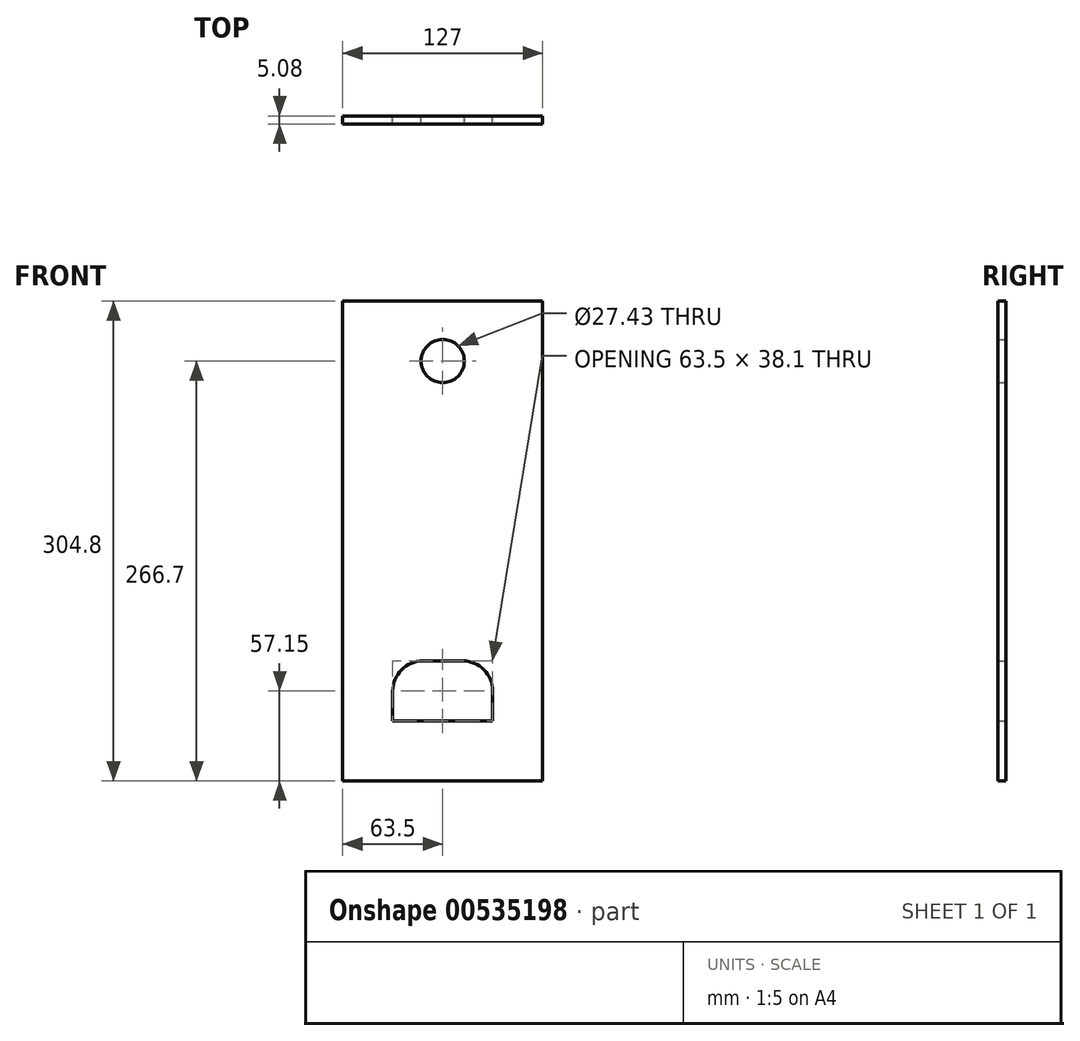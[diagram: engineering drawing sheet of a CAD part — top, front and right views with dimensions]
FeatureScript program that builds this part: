
annotation { "Feature Type Name" : "Feature", "Feature Type Description" : "" }
export const myFeature = defineFeature(function(context is Context, id is Id, definition is map)
    precondition{}
    {
        {
            var Q0;
            Q0=qCreatedBy(makeId("Front.planeOp"),FACE);
            var sketch = newSketch(context, id + "F0", { "sketchPlane" : qUnion([Q0])});
            skLineSegment(sketch, "E0.bottom", {"start": v(0, 0) * mm, "end": v(127, 0) * mm});
            skLineSegment(sketch, "E0.top", {"start": v(0, -304.8) * mm, "end": v(127, -304.8) * mm});
            skLineSegment(sketch, "E0.left", {"start": v(0, 0) * mm, "end": v(0, -304.8) * mm});
            skLineSegment(sketch, "E0.right", {"start": v(127, 0) * mm, "end": v(127, -304.8) * mm});
            skCircle(sketch, "E1", {"center": v(63.5, -38.1) * mm, "radius": 13.72 * mm});
            skLineSegment(sketch, "E2", {"start": v(63.5, 0) * mm, "end": v(63.5, -304.8) * mm, "construction": true});
            skLineSegment(sketch, "E3", {"start": v(63.5, -38.1) * mm, "end": v(127, -38.1) * mm, "construction": true});
            skLineSegment(sketch, "E4.bottom", {"start": v(31.75, -266.7) * mm, "end": v(95.25, -266.7) * mm});
            skLineSegment(sketch, "E4.top", {"start": v(50.8, -228.6) * mm, "end": v(76.2, -228.6) * mm});
            skLineSegment(sketch, "E4.left", {"start": v(31.75, -266.7) * mm, "end": v(31.75, -247.65) * mm});
            skLineSegment(sketch, "E4.right", {"start": v(95.25, -266.7) * mm, "end": v(95.25, -247.65) * mm});
            skPoint(sketch, "E5.visualSharp", {"position": v(31.75, -228.6) * mm});
            skArc(sketch, "E5.filletArc", {"start": v(50.8, -228.6) * mm, "mid": v(37.33, -234.18) * mm, "end": v(31.75, -247.65) * mm});
            skPoint(sketch, "E6.visualSharp", {"position": v(95.25, -228.6) * mm});
            skArc(sketch, "E6.filletArc", {"start": v(95.25, -247.65) * mm, "mid": v(89.67, -234.18) * mm, "end": v(76.2, -228.6) * mm});
            skSolve(sketch);
        }
        {
            var Q0;
            Q0=qSketchRegion(id+"F0",true);
            extrude(context, id + "F1", {"entities" : qUnion([Q0]), "depth" : 5.08 * mm});
        }
    });
